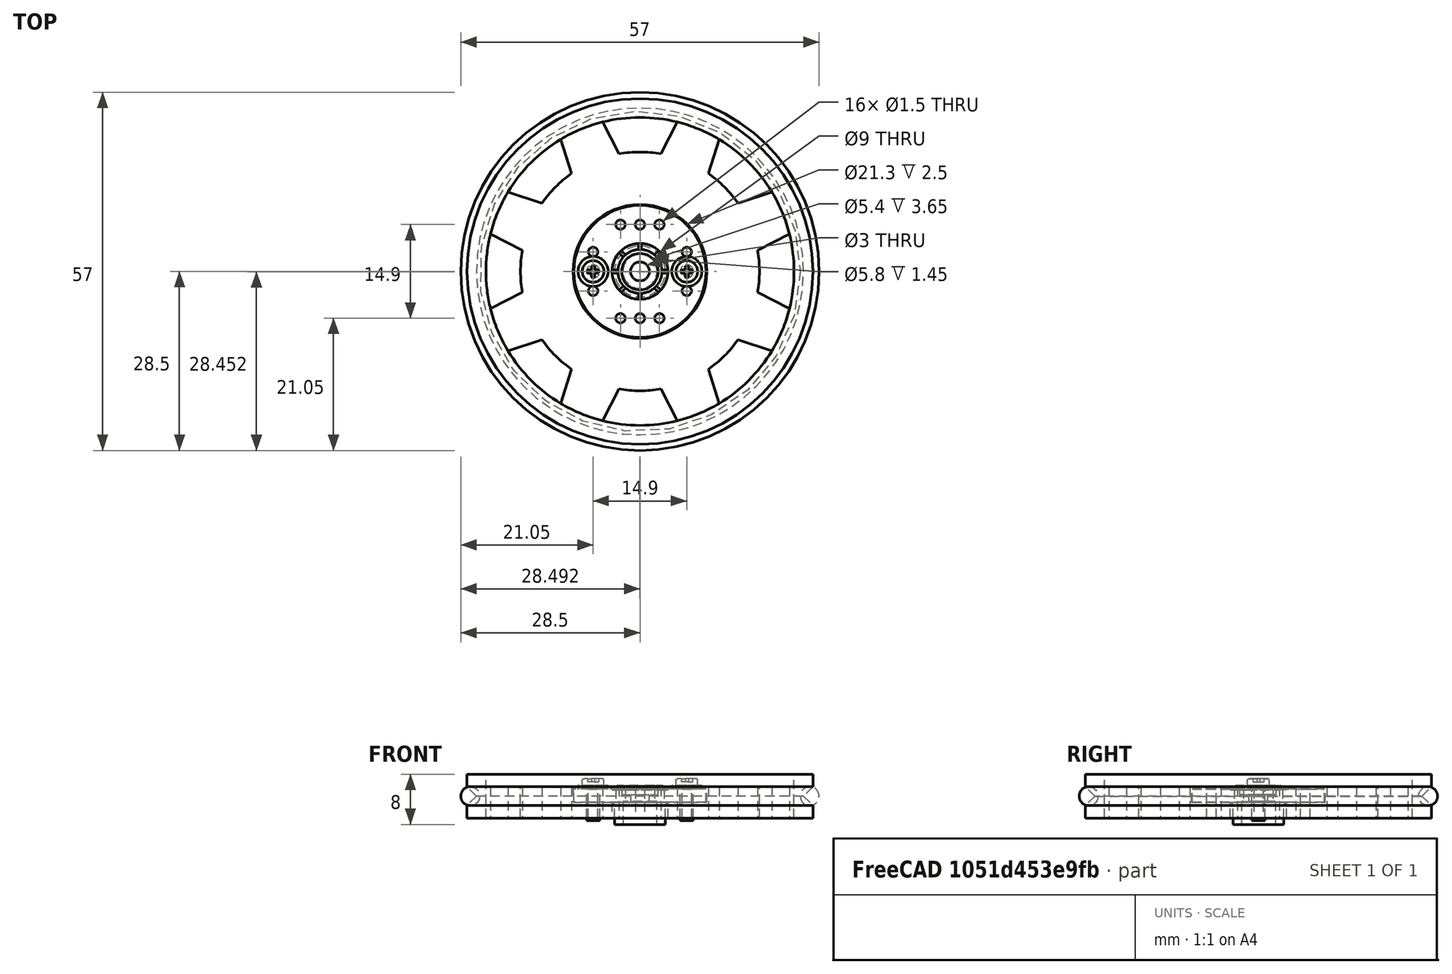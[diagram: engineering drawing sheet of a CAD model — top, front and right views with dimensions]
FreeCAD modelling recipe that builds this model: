
FCSTD DOCUMENT  (FreeCAD 0.14R3702 (Git))
Label: Miniskybot-wheel-gear-futaba3003-assembly
License: CC-BY 3.0
LicenseURL: http://creativecommons.org/licenses/by/3.0/
objects: Part::Feature×4, Part::Torus×1, Part::Compound×1
note: 6 computed .brp shape members not serialized (recipe doc carries the construction recipe); baked Part::Feature solids carry a one-line shape summary decoded from their .brp

FEATURE [Part::Feature] PolarPattern  label="Miniskybot-wheel-gear-futaba3003-final"
  Placement = pos=(0,0,0) rot=(1,0,0;1.5708rad)
  shape: bbox 55 x 55 x 7 mm, 54 faces (baked)
FEATURE [Part::Feature] Fillet  label="servo-rounded-horn"
  Placement = pos=(0,0,-4.5) rot=(1,0,0;1.5708rad)
  shape: bbox 21 x 21 x 6.2 mm, 65 faces (baked)
FEATURE [Part::Torus] Torus  label="o-ring"
  Angle1 = -180
  Angle2 = 180
  Angle3 = 360
  Radius1 = 27
  Radius2 = 1.5
FEATURE [Part::Feature] Fillet004  label="bolt-1"
  Placement = pos=(7.45,0,1.1) rot=(0,0,1;0rad)
  shape: bbox 4.8 x 4.8 x 6.7 mm, 21 faces (baked)
FEATURE [Part::Feature] Fillet005  label="bolt-2"
  Placement = pos=(-7.45,0,1.1) rot=(0,0,1;0rad)
  shape: bbox 4.8 x 4.8 x 6.7 mm, 21 faces (baked)
FEATURE [Part::Compound] Compound  label="Miniskybot-wheel-gear-futaba3003-assembly-final"
  Links = -> [PolarPattern,Fillet005,Fillet,Torus,Fillet004]
